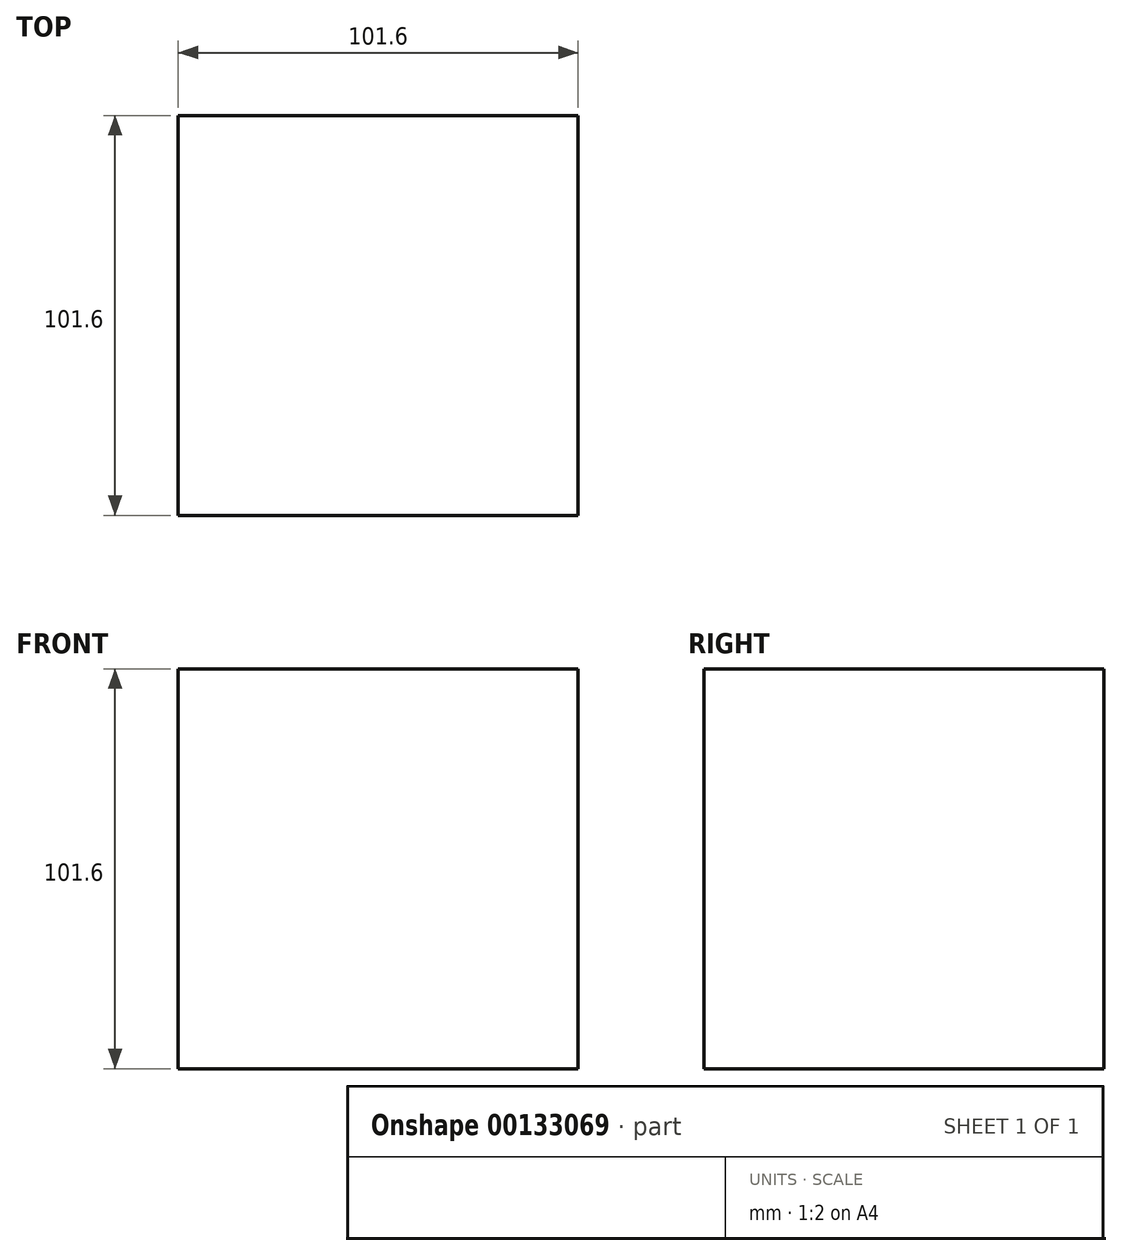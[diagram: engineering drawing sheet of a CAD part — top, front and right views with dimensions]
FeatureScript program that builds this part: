
annotation { "Feature Type Name" : "Feature", "Feature Type Description" : "" }
export const myFeature = defineFeature(function(context is Context, id is Id, definition is map)
    precondition{}
    {
        {
            var Q0;
            Q0=qCreatedBy(makeId("Front.planeOp"),FACE);
            var sketch = newSketch(context, id + "F0", { "sketchPlane" : qUnion([Q0])});
            skLineSegment(sketch, "E0.bottom", {"start": v(-50.8, 50.8) * mm, "end": v(50.8, 50.8) * mm});
            skLineSegment(sketch, "E0.top", {"start": v(-50.8, -50.8) * mm, "end": v(50.8, -50.8) * mm});
            skLineSegment(sketch, "E0.left", {"start": v(-50.8, 50.8) * mm, "end": v(-50.8, -50.8) * mm});
            skLineSegment(sketch, "E0.right", {"start": v(50.8, 50.8) * mm, "end": v(50.8, -50.8) * mm});
            skPoint(sketch, "E0.middle", {"position": v(0, 0) * mm});
            skSolve(sketch);
        }
        {
            var Q0;
            Q0=makeQuery(id+"F0.imprint","IMPRINT",FACE,{"disambiguationData":[TD([[makeQuery(id+"F0.imprint","IMPRINT",EDGE,{"derivedFrom":sQuery(id+"F0.wireOp",EDGE,"E0.bottom")}),-1.0]])]});
            extrude(context, id + "F1", {"entities" : qUnion([Q0]), "endBound" : BoundingType.SYMMETRIC, "depth" : 101.6 * mm});
        }
    });
